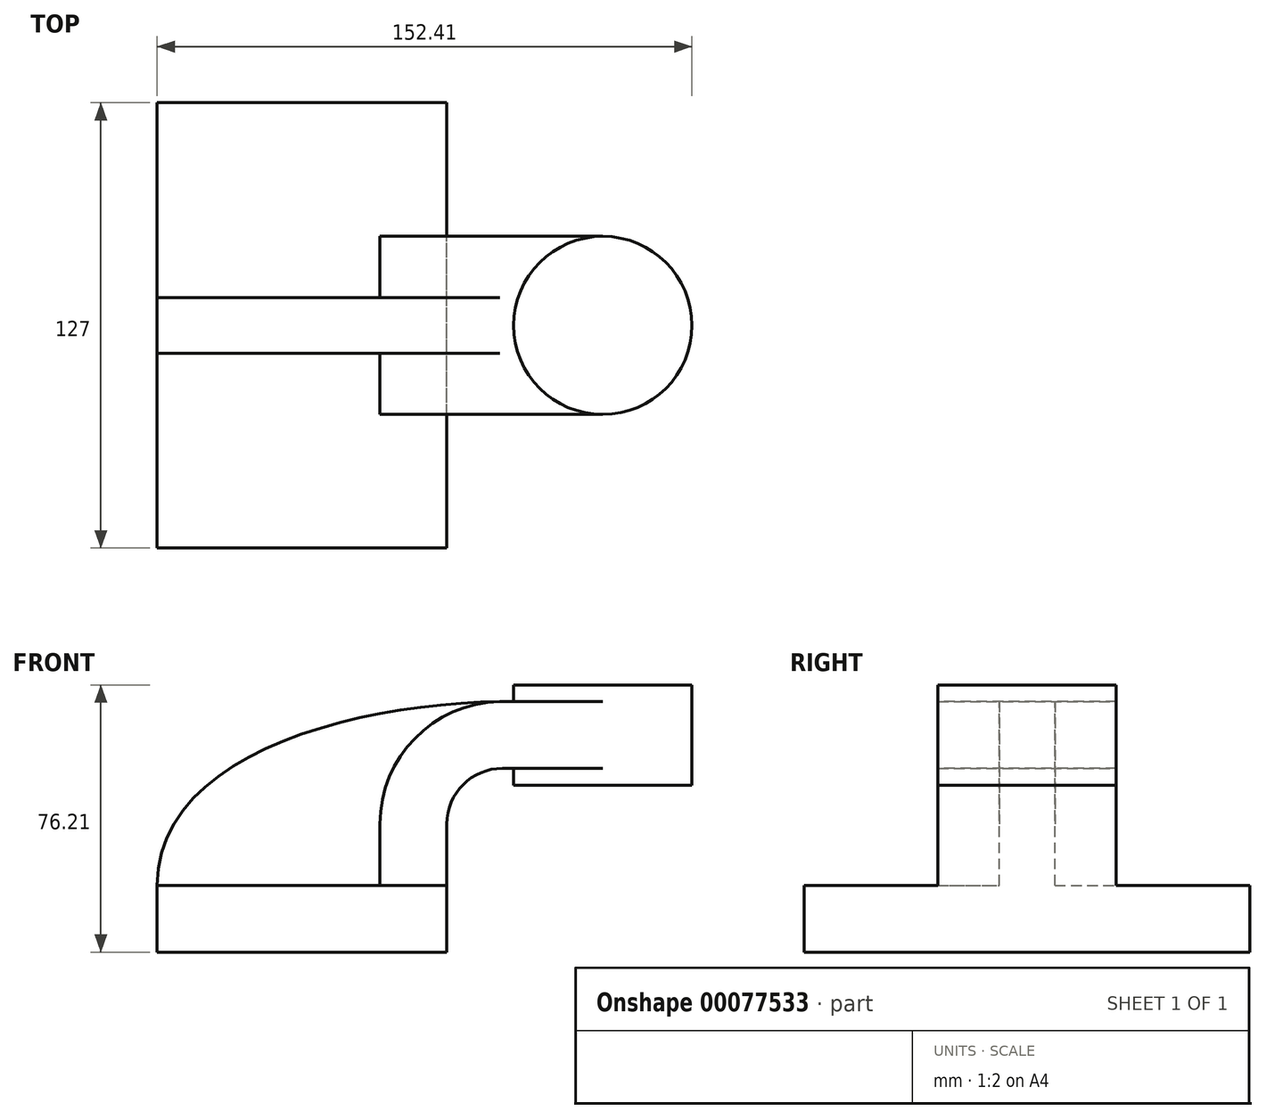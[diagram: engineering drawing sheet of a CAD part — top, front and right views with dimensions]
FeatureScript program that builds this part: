
annotation { "Feature Type Name" : "Feature", "Feature Type Description" : "" }
export const myFeature = defineFeature(function(context is Context, id is Id, definition is map)
    precondition{}
    {
        {
            var Q0;
            Q0=qCreatedBy(makeId("Front.planeOp"),FACE);
            var sketch = newSketch(context, id + "F0", { "sketchPlane" : qUnion([Q0])});
            skLineSegment(sketch, "E0.bottom", {"start": v(-41.28, -9.53) * mm, "end": v(41.28, -9.53) * mm});
            skLineSegment(sketch, "E0.top", {"start": v(-41.28, 9.53) * mm, "end": v(41.28, 9.53) * mm});
            skLineSegment(sketch, "E0.left", {"start": v(-41.28, -9.53) * mm, "end": v(-41.28, 9.53) * mm});
            skLineSegment(sketch, "E0.right", {"start": v(41.28, -9.53) * mm, "end": v(41.28, 9.53) * mm});
            skPoint(sketch, "E0.middle", {"position": v(0, 0) * mm});
            skLineSegment(sketch, "E1.bottom", {"start": v(60.33, 38.1) * mm, "end": v(111.12, 38.1) * mm});
            skLineSegment(sketch, "E1.top", {"start": v(60.32, 66.68) * mm, "end": v(111.12, 66.68) * mm});
            skLineSegment(sketch, "E1.left", {"start": v(60.32, 38.1) * mm, "end": v(60.32, 66.67) * mm});
            skLineSegment(sketch, "E1.right", {"start": v(111.12, 38.1) * mm, "end": v(111.12, 66.67) * mm});
            skPoint(sketch, "E1.middle", {"position": v(85.72, 52.39) * mm});
            skLineSegment(sketch, "E2", {"start": v(41.28, 9.52) * mm, "end": v(41.28, 27) * mm});
            skArc(sketch, "E3", {"start": v(41.27, 27) * mm, "mid": v(45.92, 38.23) * mm, "end": v(57.15, 42.88) * mm});
            skLineSegment(sketch, "E4", {"start": v(57.15, 42.88) * mm, "end": v(85.72, 42.88) * mm});
            skLineSegment(sketch, "E5.0", {"start": v(57.15, 61.93) * mm, "end": v(85.72, 61.93) * mm});
            skArc(sketch, "E5.1", {"start": v(22.22, 27) * mm, "mid": v(32.45, 51.7) * mm, "end": v(57.15, 61.93) * mm});
            skLineSegment(sketch, "E5.2", {"start": v(22.22, 9.52) * mm, "end": v(22.22, 27) * mm});
            skLineSegment(sketch, "E6", {"start": v(85.72, 38.1) * mm, "end": v(85.72, 42.88) * mm});
            skLineSegment(sketch, "E7", {"start": v(85.72, 52.39) * mm, "end": v(85.72, 61.93) * mm});
            skLineSegment(sketch, "E8", {"start": v(85.72, 66.68) * mm, "end": v(85.72, 61.93) * mm});
            skFitSpline(sketch, "E9", {"points": [v(-41.28, 9.52) * mm, v(57.15, 61.93) * mm], "startDerivative": vector(0.16, 113.23) * mm, "endDerivative": vector(123.94, 1.18) * mm});
            skLineSegment(sketch, "E10", {"start": v(85.72, 52.39) * mm, "end": v(85.72, 38.1) * mm});
            skSolve(sketch);
        }
        {
            var Q0;
            Q0=makeQuery(id+"F0.imprint","IMPRINT",FACE,{"disambiguationData":[TD([[makeQuery(id+"F0.imprint","IMPRINT",EDGE,{"derivedFrom":sQuery(id+"F0.wireOp",EDGE,"E0.bottom")}),1.0]])]});
            extrude(context, id + "F1", {"entities" : qUnion([Q0]), "endBound" : BoundingType.SYMMETRIC, "depth" : 127 * mm});
        }
        {
            var Q0;
            {var subQ6=sQuery(id+"F0.wireOp",EDGE,"E2");Q0=makeQuery(id+"F0.imprint","IMPRINT",FACE,{"disambiguationData":[TD([[makeQuery(id+"F0.imprint","IMPRINT",EDGE,{"derivedFrom":subQ6}),1.0]])]});}
            var Q1;
            {var subQ0=sQuery(id+"F0.wireOp",EDGE,"E7");Q1=makeQuery(id+"F0.imprint","IMPRINT",FACE,{"disambiguationData":[TD([[makeQuery(id+"F0.imprint","IMPRINT",EDGE,{"derivedFrom":subQ0}),1.0]])]});}
            extrude(context, id + "F2", {"entities" : qUnion([Q0, Q1]), "operationType" : NewBodyOperationType.ADD, "endBound" : BoundingType.SYMMETRIC, "depth" : 50.8 * mm});
        }
        {
            var Q0;
            {var subQ3=sQuery(id+"F0.wireOp",EDGE,"E5.2");Q0=makeQuery(id+"F0.imprint","IMPRINT",FACE,{"disambiguationData":[TD([[makeQuery(id+"F0.imprint","IMPRINT",EDGE,{"derivedFrom":subQ3}),1.0]])]});}
            extrude(context, id + "F3", {"entities" : qUnion([Q0]), "operationType" : NewBodyOperationType.ADD, "endBound" : BoundingType.SYMMETRIC, "depth" : 15.88 * mm});
        }
        {
            var Q0;
            {var subQ0=sQuery(id+"F0.wireOp",EDGE,"E1.right");Q0=makeQuery(id+"F0.imprint","IMPRINT",FACE,{"disambiguationData":[TD([[makeQuery(id+"F0.imprint","IMPRINT",EDGE,{"derivedFrom":subQ0}),1.0]])]});}
            var Q1;
            Q1=sQuery(id+"F0.wireOp",EDGE,"E10");
            revolve(context, id + "F4", {"operationType" : NewBodyOperationType.ADD, "entities" : qUnion([Q0]), "axis" : qUnion([Q1]), "revolveType" : RevolveType.FULL});
        }
    });
